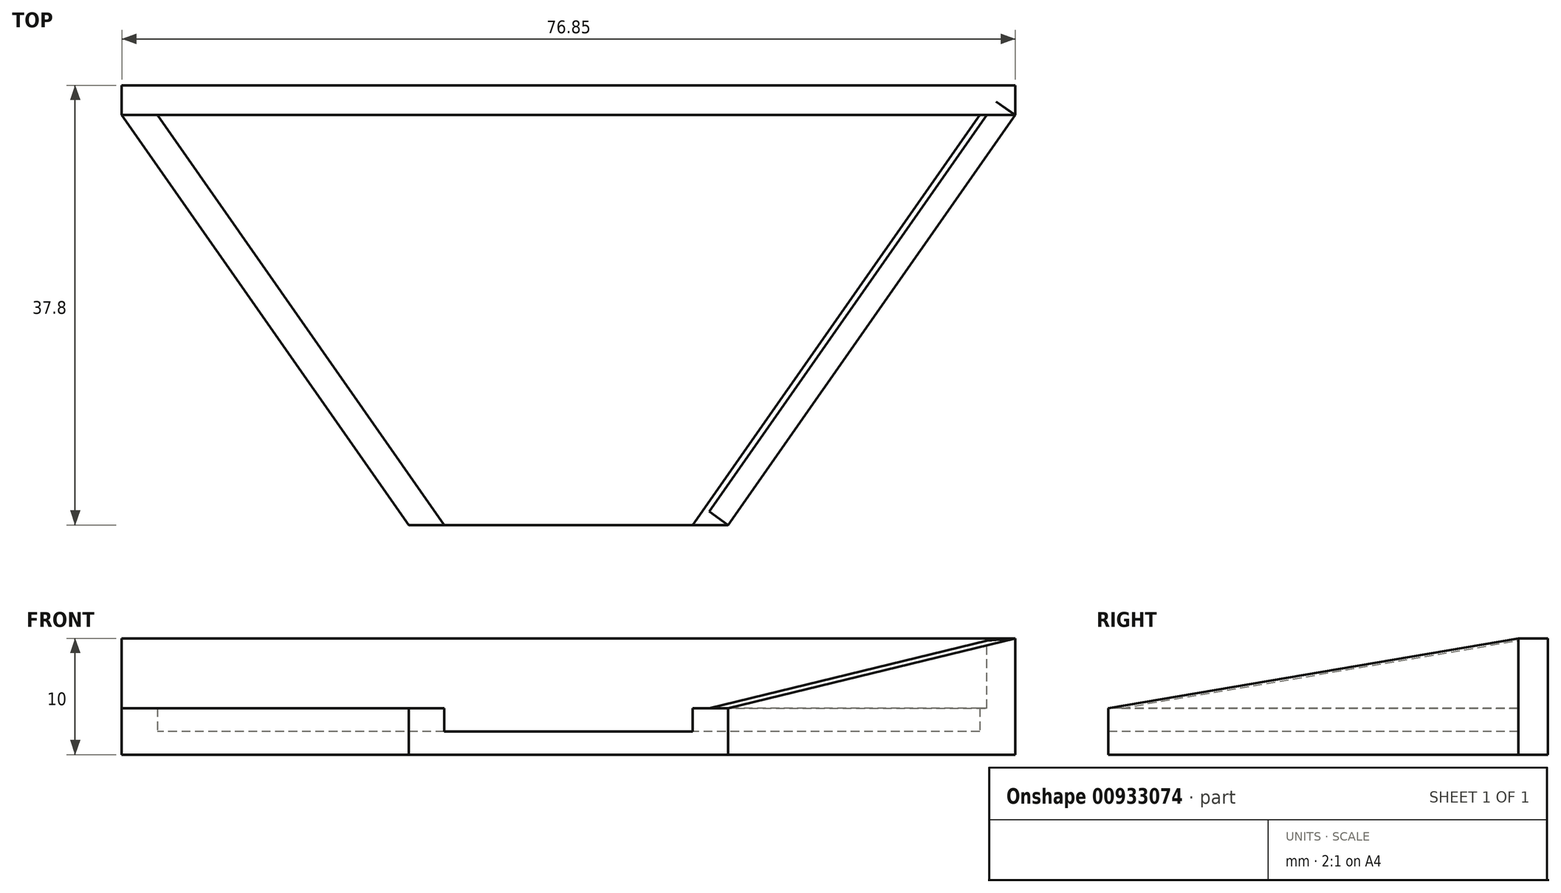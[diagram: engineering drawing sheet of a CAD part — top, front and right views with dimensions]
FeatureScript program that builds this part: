
annotation { "Feature Type Name" : "Feature", "Feature Type Description" : "" }
export const myFeature = defineFeature(function(context is Context, id is Id, definition is map)
    precondition{}
    {
        {
            var Q0;
            Q0=qCreatedBy(makeId("Top.planeOp"),FACE);
            var sketch = newSketch(context, id + "F0", { "sketchPlane" : qUnion([Q0])});
            skLineSegment(sketch, "E0", {"start": v(-12.36, 0) * mm, "end": v(15.1, 0) * mm});
            skLineSegment(sketch, "E1", {"start": v(15.1, 0) * mm, "end": v(39.8, 35.27) * mm});
            skLineSegment(sketch, "E2", {"start": v(39.8, 35.27) * mm, "end": v(-37.05, 35.27) * mm});
            skLineSegment(sketch, "E3", {"start": v(-37.05, 35.27) * mm, "end": v(-12.36, 0) * mm});
            skLineSegment(sketch, "E4", {"start": v(-37.05, 35.27) * mm, "end": v(-34, 35.27) * mm});
            skLineSegment(sketch, "E5", {"start": v(-34, 35.27) * mm, "end": v(-9.3, 0) * mm});
            skLineSegment(sketch, "E6", {"start": v(39.8, 35.27) * mm, "end": v(36.75, 35.27) * mm});
            skLineSegment(sketch, "E7", {"start": v(36.75, 35.27) * mm, "end": v(12.06, 0) * mm});
            skLineSegment(sketch, "E8", {"start": v(-37.05, 35.27) * mm, "end": v(-37.05, 37.8) * mm});
            skLineSegment(sketch, "E9", {"start": v(-37.05, 37.8) * mm, "end": v(39.8, 37.8) * mm});
            skLineSegment(sketch, "E10", {"start": v(39.8, 37.8) * mm, "end": v(39.8, 35.27) * mm});
            skLineSegment(sketch, "E11", {"start": v(36.75, 35.27) * mm, "end": v(36.75, 37.8) * mm});
            skLineSegment(sketch, "E12", {"start": v(-34, 35.27) * mm, "end": v(-34, 37.8) * mm});
            skSolve(sketch);
        }
        {
            var Q0;
            {var subQ0=sQuery(id+"F0.wireOp",EDGE,"E5");Q0=makeQuery(id+"F0.imprint","IMPRINT",FACE,{"disambiguationData":[TD([[makeQuery(id+"F0.imprint","IMPRINT",EDGE,{"derivedFrom":subQ0}),1.0]])]});}
            extrude(context, id + "F1", {"entities" : qUnion([Q0]), "depth" : 2 * mm, "offsetDistance" : 25 * mm});
        }
        {
            var Q0;
            {var subQ2=sQuery(id+"F0.wireOp",EDGE,"E3");Q0=makeQuery(id+"F0.imprint","IMPRINT",FACE,{"disambiguationData":[TD([[makeQuery(id+"F0.imprint","IMPRINT",EDGE,{"derivedFrom":subQ2}),1.0]])]});}
            var Q1;
            {var subQ0=sQuery(id+"F0.wireOp",EDGE,"E1");Q1=makeQuery(id+"F0.imprint","IMPRINT",FACE,{"disambiguationData":[TD([[makeQuery(id+"F0.imprint","IMPRINT",EDGE,{"derivedFrom":subQ0}),1.0]])]});}
            extrude(context, id + "F2", {"entities" : qUnion([Q0, Q1]), "operationType" : NewBodyOperationType.ADD, "depth" : 4 * mm, "offsetDistance" : 25 * mm});
        }
        {
            var Q0;
            {var subQ0=sQuery(id+"F0.wireOp",EDGE,"E11");Q0=makeQuery(id+"F0.imprint","IMPRINT",FACE,{"disambiguationData":[TD([[makeQuery(id+"F0.imprint","IMPRINT",EDGE,{"derivedFrom":subQ0}),1.0]])]});}
            extrude(context, id + "F3", {"entities" : qUnion([Q0]), "depth" : 10 * mm, "offsetDistance" : 25 * mm});
        }
        {
            var Q0;
            {var subQ0=sQuery(id+"F0.wireOp",EDGE,"E10");Q0=makeQuery(id+"F0.imprint","IMPRINT",FACE,{"disambiguationData":[TD([[makeQuery(id+"F0.imprint","IMPRINT",EDGE,{"derivedFrom":subQ0}),-1.0]])]});}
            var Q1;
            {var subQ0=sQuery(id+"F0.wireOp",EDGE,"E8");Q1=makeQuery(id+"F0.imprint","IMPRINT",FACE,{"disambiguationData":[TD([[makeQuery(id+"F0.imprint","IMPRINT",EDGE,{"derivedFrom":subQ0}),-1.0]])]});}
            extrude(context, id + "F4", {"entities" : qUnion([Q0, Q1]), "operationType" : NewBodyOperationType.ADD, "depth" : 10 * mm, "offsetDistance" : 25 * mm});
        }
        {
            var Q0;
            Q0=makeQuery(id+"F2.opExtrude","SWEPT_FACE",FACE,{"disambiguationData":[OSD([sQuery(id+"F0.wireOp",EDGE,"E1")])]});
            var sketch = newSketch(context, id + "F5", { "sketchPlane" : qUnion([Q0])});
            skLineSegment(sketch, "E13", {"start": v(8.67, 4) * mm, "end": v(51.72, 10) * mm});
            skLineSegment(sketch, "E14", {"start": v(51.72, 10) * mm, "end": v(51.72, 4) * mm});
            skLineSegment(sketch, "E15", {"start": v(51.72, 4) * mm, "end": v(8.67, 4) * mm});
            skSolve(sketch);
        }
        {
            var Q0;
            Q0=makeQuery(id+"F5.imprint","IMPRINT",FACE,{"disambiguationData":[TD([[makeQuery(id+"F5.imprint","IMPRINT",EDGE,{"derivedFrom":sQuery(id+"F5.wireOp",EDGE,"E13")}),-1.0]])]});
            extrude(context, id + "F6", {"entities" : qUnion([Q0]), "operationType" : NewBodyOperationType.ADD, "oppositeDirection" : true, "depth" : 2 * mm, "offsetDistance" : 25 * mm});
        }
    });
